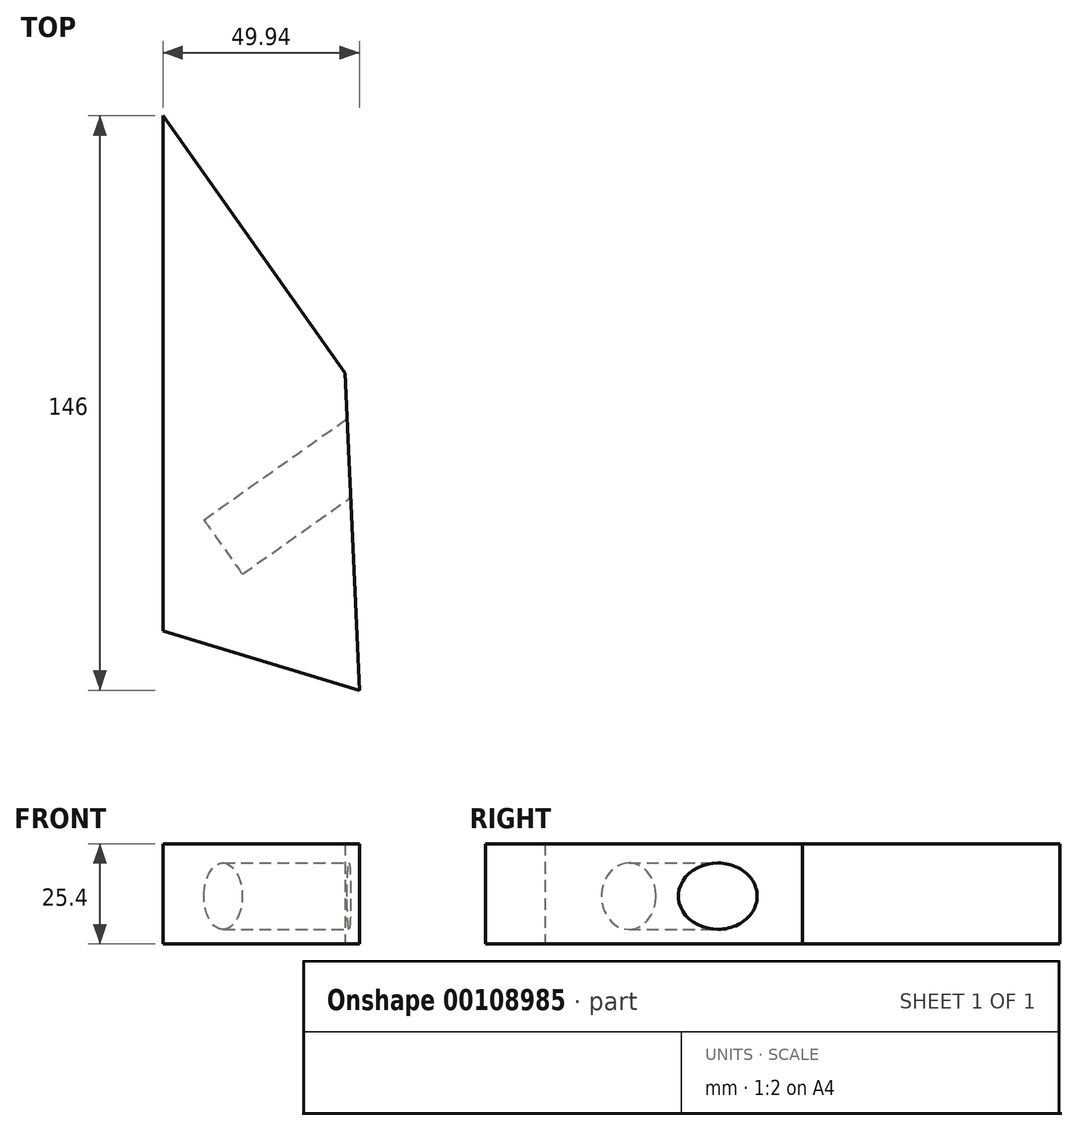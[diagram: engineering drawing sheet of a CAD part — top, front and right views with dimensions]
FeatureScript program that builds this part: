
annotation { "Feature Type Name" : "Feature", "Feature Type Description" : "" }
export const myFeature = defineFeature(function(context is Context, id is Id, definition is map)
    precondition{}
    {
        {
            var Q0;
            Q0=qCreatedBy(makeId("Top.planeOp"),FACE);
            var sketch = newSketch(context, id + "F2", { "sketchPlane" : qUnion([Q0])});
            skLineSegment(sketch, "E0", {"start": v(0, 0) * mm, "end": v(0, 130.9) * mm});
            skLineSegment(sketch, "E1", {"start": v(0, 130.9) * mm, "end": v(46.3, 65.45) * mm});
            skPoint(sketch, "E1.endSnap0", {"position": v(0, 65.45) * mm});
            skLineSegment(sketch, "E2", {"start": v(46.3, 65.45) * mm, "end": v(49.94, -15.1) * mm});
            skLineSegment(sketch, "E3", {"start": v(49.94, -15.1) * mm, "end": v(0, 0) * mm});
            skSolve(sketch);
        }
        {
            var Q0;
            Q0 = qSketchRegion(id + "F2", true);
            extrude(context, id + "F0", {"entities" : qUnion([Q0]), "depth" : 25.4 * mm});
        }
        {
            var Q0;
            Q0=makeQuery(id+"F0.opExtrude","SWEPT_FACE",FACE,{"disambiguationData":[OSD([sQuery(id+"F2.wireOp",EDGE,"E1")])]});
            var sketch = newSketch(context, id + "F3", { "sketchPlane" : qUnion([Q0])});
            skCircle(sketch, "E4", {"center": v(8.55, 12.1) * mm, "radius": 8.44 * mm});
            skSolve(sketch);
        }
        {
            var Q0;
            Q0=makeQuery(id+"F3.imprint","IMPRINT",FACE,{"disambiguationData":[TD([[makeQuery(id+"F3.imprint","IMPRINT",EDGE,{"derivedFrom":sQuery(id+"F3.wireOp",EDGE,"E4")}),1.0]])]});
            extrude(context, id + "F1", {"entities" : qUnion([Q0]), "operationType" : NewBodyOperationType.REMOVE, "oppositeDirection" : true, "depth" : 50.8 * mm});
        }
    });
